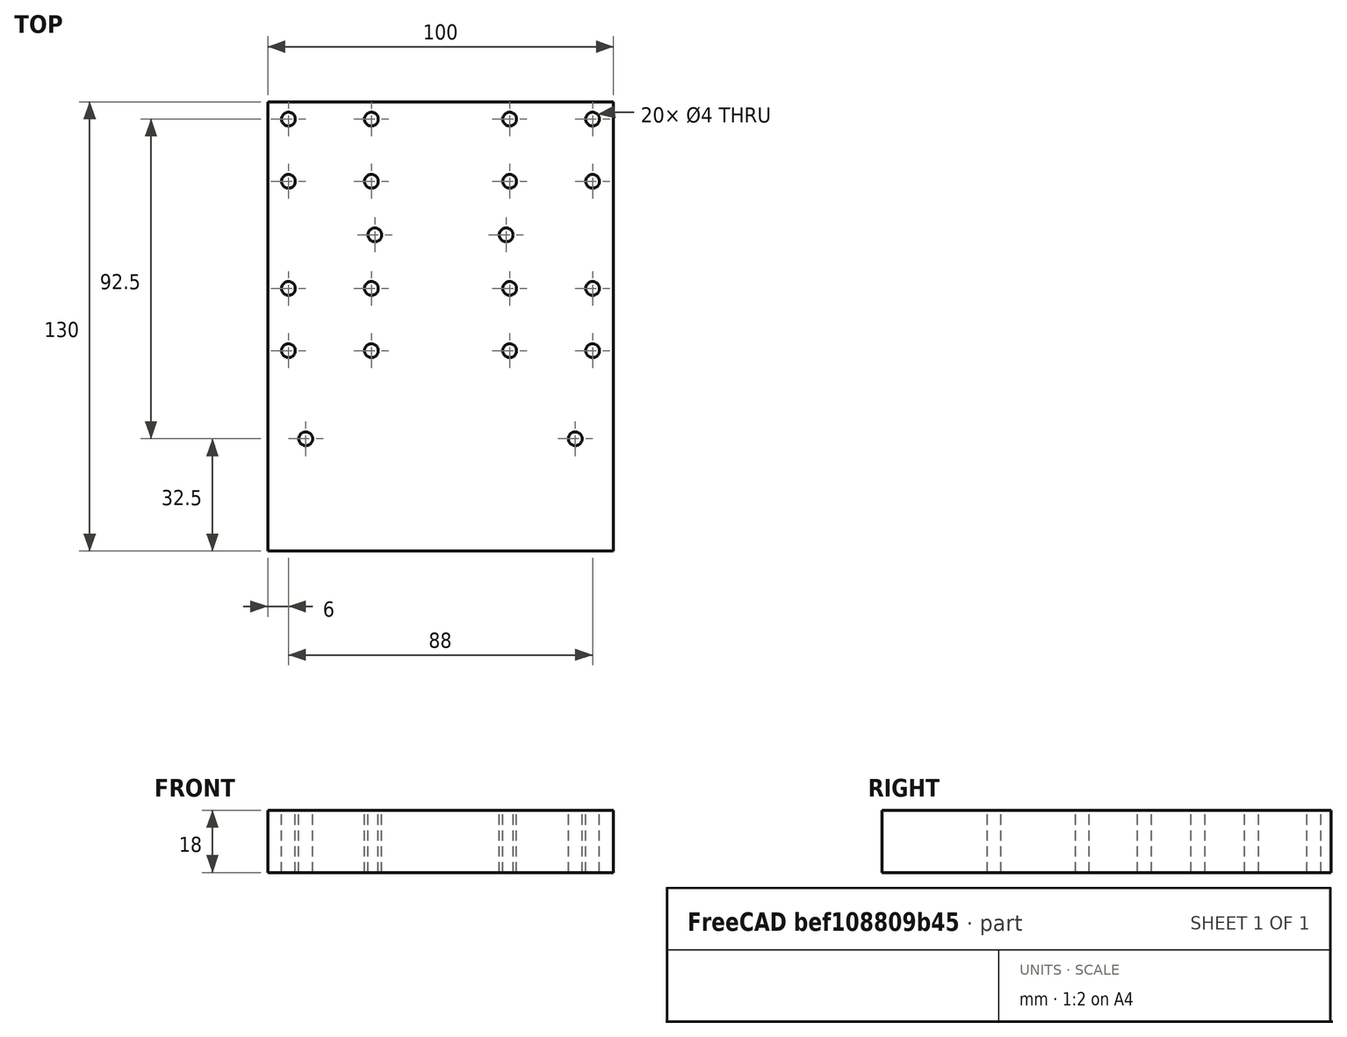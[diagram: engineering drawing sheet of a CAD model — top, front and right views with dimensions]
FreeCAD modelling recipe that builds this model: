
FCSTD DOCUMENT  (FreeCAD 0.17R13541 (Git))
Label: Z-PortaTaladro
License: All rights reserved
LicenseURL: http://en.wikipedia.org/wiki/All_rights_reserved
objects: Part::Cylinder×10, Part::Cut×4, Part::MultiFuse×3, Part::Box×1, Part::Mirroring×1
note: 19 computed .brp shape members not serialized (recipe doc carries the construction recipe); baked Part::Feature solids carry a one-line shape summary decoded from their .brp

FEATURE [Part::Box] Box  label="Base"
  AttacherType = Attacher::AttachEngine3D
  Height = 18
  Length = 50
  Width = 130
FEATURE [Part::Cylinder] Cylinder  label="Cilindro"
  Angle = 360
  AttacherType = Attacher::AttachEngine3D
  Height = 25
  Placement = pos=(6,58,0) rot=(0,0,1;0rad)
  Radius = 2
FEATURE [Part::Cylinder] Cylinder001  label="Cilindro001"
  Angle = 360
  AttacherType = Attacher::AttachEngine3D
  Height = 25
  Placement = pos=(30,58,0) rot=(0,0,1;0rad)
  Radius = 2
FEATURE [Part::Cylinder] Cylinder002  label="Cilindro002"
  Angle = 360
  AttacherType = Attacher::AttachEngine3D
  Height = 25
  Placement = pos=(6,76,0) rot=(0,0,1;0rad)
  Radius = 2
FEATURE [Part::Cylinder] Cylinder003  label="Cilindro003"
  Angle = 360
  AttacherType = Attacher::AttachEngine3D
  Height = 25
  Placement = pos=(30,76,0) rot=(0,0,1;0rad)
  Radius = 2
FEATURE [Part::MultiFuse] Fusion  label="Huecos"
  Refine = true
  Shapes = -> [Cylinder003,Cylinder002,Cylinder001,Cylinder]
FEATURE [Part::Cylinder] Cylinder004  label="Cilindro004"
  Angle = 360
  AttacherType = Attacher::AttachEngine3D
  Height = 25
  Placement = pos=(11,32.5,0) rot=(0,0,1;0rad)
  Radius = 2
FEATURE [Part::Cylinder] Cylinder005  label="Cilindro005"
  Angle = 360
  AttacherType = Attacher::AttachEngine3D
  Height = 25
  Placement = pos=(31,91.5,0) rot=(0,0,1;0rad)
  Radius = 2
FEATURE [Part::Cylinder] Cylinder006  label="Cilindro006"
  Angle = 360
  AttacherType = Attacher::AttachEngine3D
  Height = 25
  Placement = pos=(6,58,0) rot=(0,0,1;0rad)
  Radius = 2
FEATURE [Part::Cylinder] Cylinder007  label="Cilindro007"
  Angle = 360
  AttacherType = Attacher::AttachEngine3D
  Height = 25
  Placement = pos=(6,76,0) rot=(0,0,1;0rad)
  Radius = 2
FEATURE [Part::Cylinder] Cylinder008  label="Cilindro008"
  Angle = 360
  AttacherType = Attacher::AttachEngine3D
  Height = 25
  Placement = pos=(30,58,0) rot=(0,0,1;0rad)
  Radius = 2
FEATURE [Part::Cylinder] Cylinder009  label="Cilindro009"
  Angle = 360
  AttacherType = Attacher::AttachEngine3D
  Height = 25
  Placement = pos=(30,76,0) rot=(0,0,1;0rad)
  Radius = 2
FEATURE [Part::MultiFuse] Fusion001  label="Huecos001"
  Placement = pos=(0,49,0) rot=(0,0,1;0rad)
  Refine = true
  Shapes = -> [Cylinder009,Cylinder007,Cylinder008,Cylinder006]
FEATURE [Part::Cut] Cut
  Base = -> Box
  Refine = true
  Tool = -> Cylinder004
FEATURE [Part::Cut] Cut001
  Base = -> Cut
  Refine = true
  Tool = -> Fusion
FEATURE [Part::Cut] Cut002
  Base = -> Cut001
  Refine = true
  Tool = -> Cylinder005
FEATURE [Part::Cut] Cut003  label="Izquierda"
  Base = -> Cut002
  Refine = true
  Tool = -> Fusion001
FEATURE [Part::Mirroring] mirror  label="Mirror of Izquierda"
  Base = (50,0,0.197234)
  Normal = (0.71,0,0)
  Source = -> Cut003
FEATURE [Part::MultiFuse] Fusion002
  Refine = true
  Shapes = -> [mirror,Cut003]
